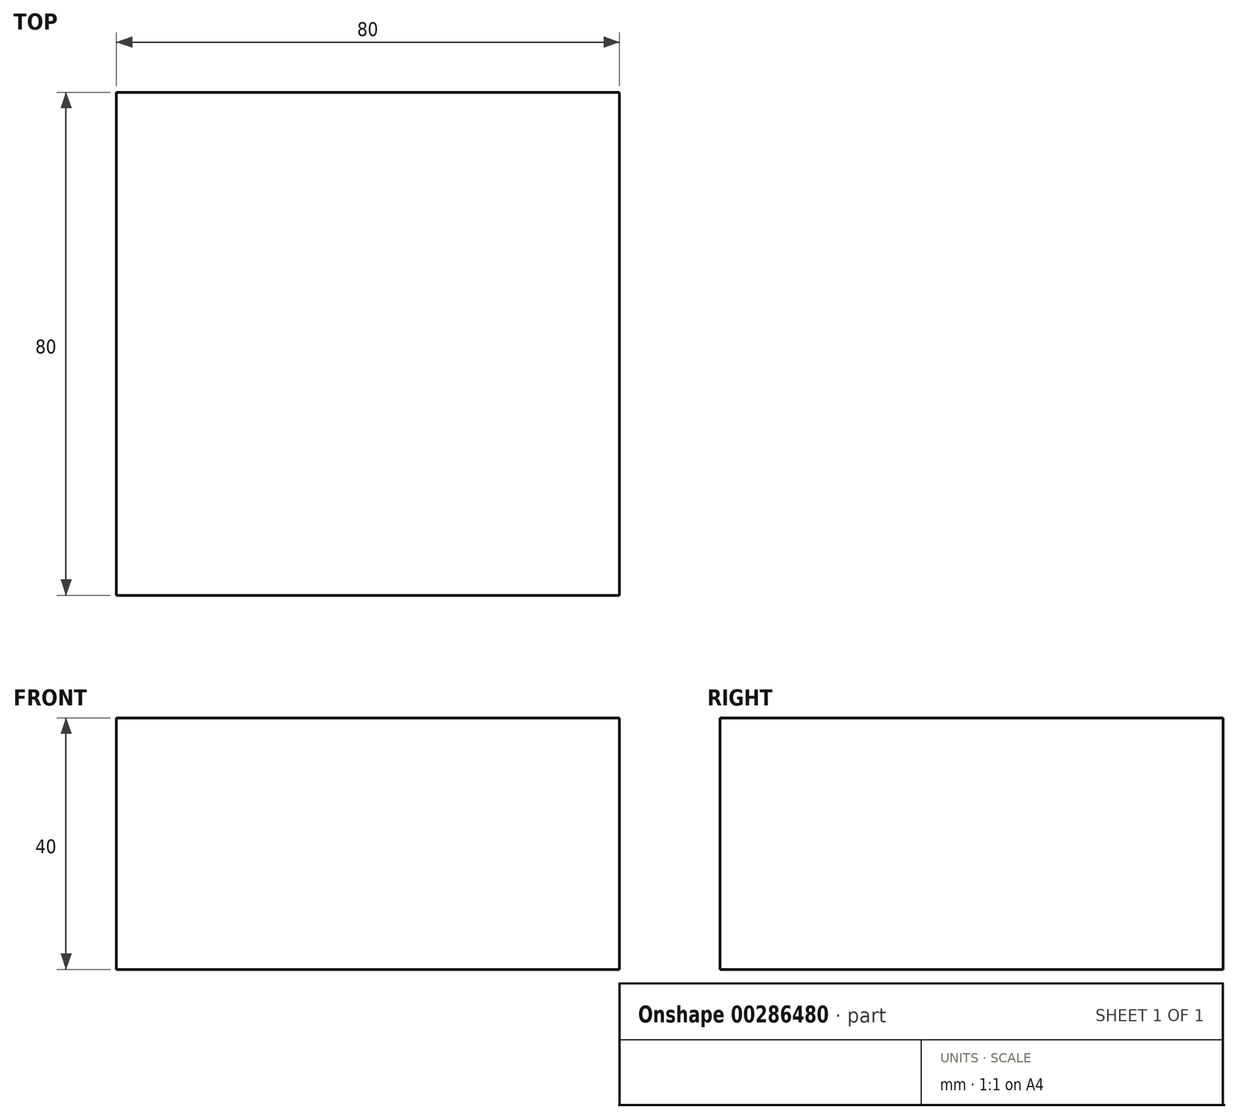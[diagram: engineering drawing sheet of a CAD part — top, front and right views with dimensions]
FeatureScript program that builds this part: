
annotation { "Feature Type Name" : "Feature", "Feature Type Description" : "" }
export const myFeature = defineFeature(function(context is Context, id is Id, definition is map)
    precondition{}
    {
        {
            var Q0;
            Q0=qCreatedBy(makeId("Top.planeOp"), FACE);
            var sketch = newSketch(context, id + "F0", { "sketchPlane" : qUnion([Q0])});
            skLineSegment(sketch, "E0.bottom", {"start": v(40, 40) * mm, "end": v(-40, 40) * mm});
            skLineSegment(sketch, "E0.top", {"start": v(40, -40) * mm, "end": v(-40, -40) * mm});
            skLineSegment(sketch, "E0.left", {"start": v(40, 40) * mm, "end": v(40, -40) * mm});
            skLineSegment(sketch, "E0.right", {"start": v(-40, 40) * mm, "end": v(-40, -40) * mm});
            skPoint(sketch, "E0.middle", {"position": v(0, 0) * mm});
            skSolve(sketch);
        }
        {
            var Q0;
            Q0 = qSketchRegion(id + "F0", true);
            extrude(context, id + "F1", {"entities" : qUnion([Q0]), "oppositeDirection" : true, "depth" : 40 * mm, "offsetDistance" : 25 * mm});
        }
    });
